# Revit family: xxxxFaucet-Lavatory-American_Standard-Studio_S-7105121_Series
name_source: partatom
category: Plumbing Fixtures
units: mm (PartAtom-declared; Revit-internal decimal feet)

## family parameters
Always vertical = No
Cut with Voids When Loaded = No
OmniClass Number = 23.45.55.14
OmniClass Title = Single Faucets
Part Type = Normal
Room Calculation Point = No
Round Connector Dimension = Use Diameter
Shared = Yes
Work Plane-Based = Yes

## types (3) — shared parameters
2064101P 4" Deck Plate = No
ADA Compliant = Yes
ANSI A117.1 = Yes
ASME A112.18.1/CSA B125.1 = Yes
Assembly Code = D2020300
CSA B125.1 = Yes
CW Connection = No
CWFU = 1.5
Default Elevation = 0"
Description = Studio® S Single Hole Lever Handle Bathroom Faucet 1.2 gpm/ 4.5 L/min
EPA WaterSense® Certified = Yes
Flow Rate = 1.2 gpm/4.5 Lpm
HW Connection = No
HWFU = 1.5
Height = 7"
Installation Instruction Link = https://americanstandard.box.com
Installation Type = Deck Mounted
Length = 7 5/16"
Manufacturer = American Standard
NSF 372 = Yes
NSF 61/Section 9 = Yes
No Deck Plate = Yes
Price = Prices may vary. Please consult Manufacturer Representative for most up-to-date price list.
Product Page URL = https://www.americanstandard.ca
Revised Date = 06/06/2022
Tempered Water Connection = Yes
Tempered Water Connection Diameter = 3/8"
URL = https://www.americanstandard.ca
Vent Connection = No
WFU = 2
Warranty Information = Limited lifetime warranty – Your assurance of quality
Waste Connection = No
Width = 1 1/4"

## per-type parameters (varying)
| type | Finish | Material |
| 7105121.002 | Brass-American Standard-002-Polished Chrome | Brass-American Standard-002-Polished Chrome |
| 7105121.243 | Brass-American Standard-243-Matte Black | Brass-American Standard-243-Matte Black |
| 7105121.295 | Brass-American Standard-295-Brushed Nickel | Brass-American Standard-295-Brushed Nickel |

note: column(s) folded — value = type name in every type: Model

## geometry (parser evidence)
native form markers: Sweep x2
no freeform markers — native parametric forms only
